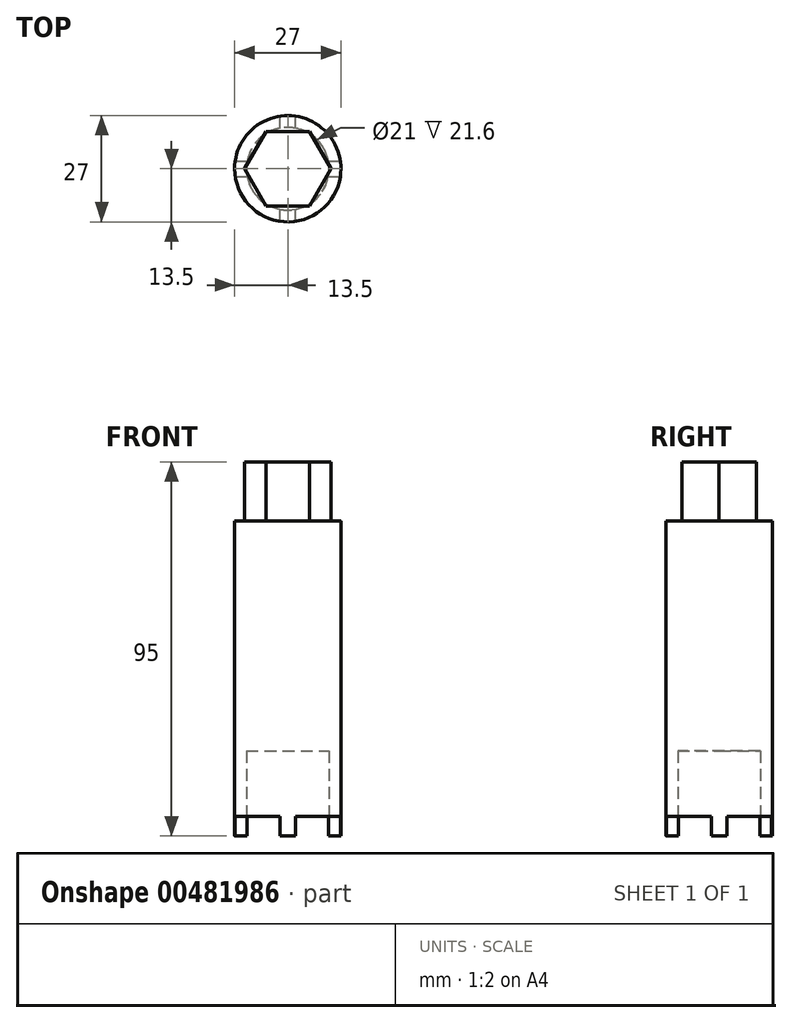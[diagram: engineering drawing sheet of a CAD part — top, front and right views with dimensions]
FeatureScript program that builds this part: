
annotation { "Feature Type Name" : "Feature", "Feature Type Description" : "" }
export const myFeature = defineFeature(function(context is Context, id is Id, definition is map)
    precondition{}
    {
        {
            var Q0;
            Q0=qCreatedBy(makeId("Top.planeOp"),FACE);
            var sketch = newSketch(context, id + "F0", { "sketchPlane" : qUnion([Q0])});
            skCircle(sketch, "E0.cCircle", {"center": v(0, 0) * mm, "radius": 9.5 * mm, "construction": true});
            skLineSegment(sketch, "E0.0", {"start": v(-10.97, 0) * mm, "end": v(-5.48, 9.5) * mm});
            skLineSegment(sketch, "E0.1", {"start": v(-5.48, 9.5) * mm, "end": v(5.48, 9.5) * mm});
            skLineSegment(sketch, "E0.2", {"start": v(5.48, 9.5) * mm, "end": v(10.97, 0) * mm});
            skLineSegment(sketch, "E0.3", {"start": v(10.97, 0) * mm, "end": v(5.48, -9.5) * mm});
            skLineSegment(sketch, "E0.4", {"start": v(5.48, -9.5) * mm, "end": v(-5.48, -9.5) * mm});
            skLineSegment(sketch, "E0.5", {"start": v(-5.48, -9.5) * mm, "end": v(-10.97, 0) * mm});
            skPoint(sketch, "E0.0.midPoint", {"position": v(-8.23, 4.75) * mm});
            skSolve(sketch);
        }
        {
            var Q0;
            Q0 = qSketchRegion(id + "F0", true);
            extrude(context, id + "F1", {"entities" : qUnion([Q0]), "depth" : 15 * mm});
        }
        {
            var Q0;
            Q0=makeQuery(id+"F1.opExtrude","CAP_FACE",FACE,{"disambiguationData":[OSD([sQuery(id+"F0.wireOp",EDGE,"E0.0"),sQuery(id+"F0.wireOp",EDGE,"E0.1"),sQuery(id+"F0.wireOp",EDGE,"E0.2"),sQuery(id+"F0.wireOp",EDGE,"E0.3"),sQuery(id+"F0.wireOp",EDGE,"E0.4"),sQuery(id+"F0.wireOp",EDGE,"E0.5")])],"isStart":true});
            var sketch = newSketch(context, id + "F2", { "sketchPlane" : qUnion([Q0])});
            skCircle(sketch, "E1", {"center": v(0, 0) * mm, "radius": 13.5 * mm});
            skSolve(sketch);
        }
        {
            var Q0;
            Q0 = qSketchRegion(id + "F2", true);
            extrude(context, id + "F3", {"entities" : qUnion([Q0]), "operationType" : NewBodyOperationType.ADD, "depth" : 80 * mm});
        }
        {
            var Q0;
            Q0=makeQuery(id+"F3.opExtrude","CAP_FACE",FACE,{"disambiguationData":[OSD([sQuery(id+"F2.wireOp",EDGE,"E1")])],"isStart":false});
            var sketch = newSketch(context, id + "F4", { "sketchPlane" : qUnion([Q0])});
            skCircle(sketch, "E2", {"center": v(0, 0) * mm, "radius": 10.5 * mm});
            skSolve(sketch);
        }
        {
            var Q0;
            Q0=makeQuery(id+"F4.imprint","IMPRINT",FACE,{"disambiguationData":[TD([[makeQuery(id+"F4.imprint","IMPRINT",EDGE,{"derivedFrom":sQuery(id+"F4.wireOp",EDGE,"E2")}),1.0]])]});
            extrude(context, id + "F5", {"entities" : qUnion([Q0]), "operationType" : NewBodyOperationType.REMOVE, "oppositeDirection" : true, "depth" : 21.6 * mm});
        }
        {
            var Q0;
            Q0=makeQuery(id+"F3.opExtrude","CAP_FACE",FACE,{"disambiguationData":[OSD([sQuery(id+"F2.wireOp",EDGE,"E1")])],"isStart":false});
            var sketch = newSketch(context, id + "F6", { "sketchPlane" : qUnion([Q0])});
            skArc(sketch, "E3", {"start": v(2, -10.3) * mm, "mid": v(7.42, -7.42) * mm, "end": v(10.3, -2) * mm});
            skArc(sketch, "E4", {"start": v(2, -13.35) * mm, "mid": v(9.55, -9.55) * mm, "end": v(13.35, -2) * mm});
            skLineSegment(sketch, "E5", {"start": v(0, 0) * mm, "end": v(-19.29, 0) * mm, "construction": true});
            skLineSegment(sketch, "E6", {"start": v(-13.35, -2) * mm, "end": v(-10.3, -2) * mm});
            skLineSegment(sketch, "E7.MirrorCS", {"start": v(-13.35, 2) * mm, "end": v(-10.3, 2) * mm});
            skLineSegment(sketch, "E8", {"start": v(0, 0) * mm, "end": v(0, 15.04) * mm, "construction": true});
            skLineSegment(sketch, "E9", {"start": v(-2, 13.35) * mm, "end": v(-2, 10.3) * mm});
            skLineSegment(sketch, "E10.MirrorCS", {"start": v(2, 13.35) * mm, "end": v(2, 10.3) * mm});
            skPoint(sketch, "E11.orphan", {"position": v(-2, -17.27) * mm});
            skPoint(sketch, "E12.orphan", {"position": v(2, -17.27) * mm});
            skLineSegment(sketch, "E13.trimOffspring", {"start": v(2, -10.3) * mm, "end": v(2, -13.35) * mm});
            skLineSegment(sketch, "E14.trimOffspring", {"start": v(10.3, 2) * mm, "end": v(13.35, 2) * mm});
            skLineSegment(sketch, "E15.trimOffspring", {"start": v(10.3, -2) * mm, "end": v(13.35, -2) * mm});
            skLineSegment(sketch, "E16.trimOffspring", {"start": v(-2, -10.3) * mm, "end": v(-2, -13.35) * mm});
            skArc(sketch, "E17.trimOffspring", {"start": v(-13.35, -2) * mm, "mid": v(-9.55, -9.55) * mm, "end": v(-2, -13.35) * mm});
            skArc(sketch, "E18.trimOffspring", {"start": v(-10.3, -2) * mm, "mid": v(-7.42, -7.42) * mm, "end": v(-2, -10.3) * mm});
            skArc(sketch, "E19.trimOffspring", {"start": v(-2, 10.3) * mm, "mid": v(-7.42, 7.42) * mm, "end": v(-10.3, 2) * mm});
            skArc(sketch, "E20.trimOffspring", {"start": v(-2, 13.35) * mm, "mid": v(-9.55, 9.55) * mm, "end": v(-13.35, 2) * mm});
            skArc(sketch, "E21.trimOffspring", {"start": v(10.3, 2) * mm, "mid": v(7.42, 7.42) * mm, "end": v(2, 10.3) * mm});
            skArc(sketch, "E22.trimOffspring", {"start": v(13.35, 2) * mm, "mid": v(9.55, 9.55) * mm, "end": v(2, 13.35) * mm});
            skSolve(sketch);
        }
        {
            var Q0;
            Q0=makeQuery(id+"F6.imprint","IMPRINT",FACE,{"disambiguationData":[TD([[makeQuery(id+"F6.imprint","IMPRINT",EDGE,{"derivedFrom":sQuery(id+"F6.wireOp",EDGE,"E3")}),-1.0]])]});
            var Q1;
            Q1=makeQuery(id+"F6.imprint","IMPRINT",FACE,{"disambiguationData":[TD([[makeQuery(id+"F6.imprint","IMPRINT",EDGE,{"derivedFrom":sQuery(id+"F6.wireOp",EDGE,"E6")}),-1.0]])]});
            var Q2;
            Q2=makeQuery(id+"F6.imprint","IMPRINT",FACE,{"disambiguationData":[TD([[makeQuery(id+"F6.imprint","IMPRINT",EDGE,{"derivedFrom":sQuery(id+"F6.wireOp",EDGE,"E7.MirrorCS")}),1.0]])]});
            var Q3;
            Q3=makeQuery(id+"F6.imprint","IMPRINT",FACE,{"disambiguationData":[TD([[makeQuery(id+"F6.imprint","IMPRINT",EDGE,{"derivedFrom":sQuery(id+"F6.wireOp",EDGE,"E10.MirrorCS")}),1.0]])]});
            extrude(context, id + "F7", {"entities" : qUnion([Q0, Q1, Q2, Q3]), "operationType" : NewBodyOperationType.REMOVE, "oppositeDirection" : true, "depth" : 5 * mm});
        }
    });
